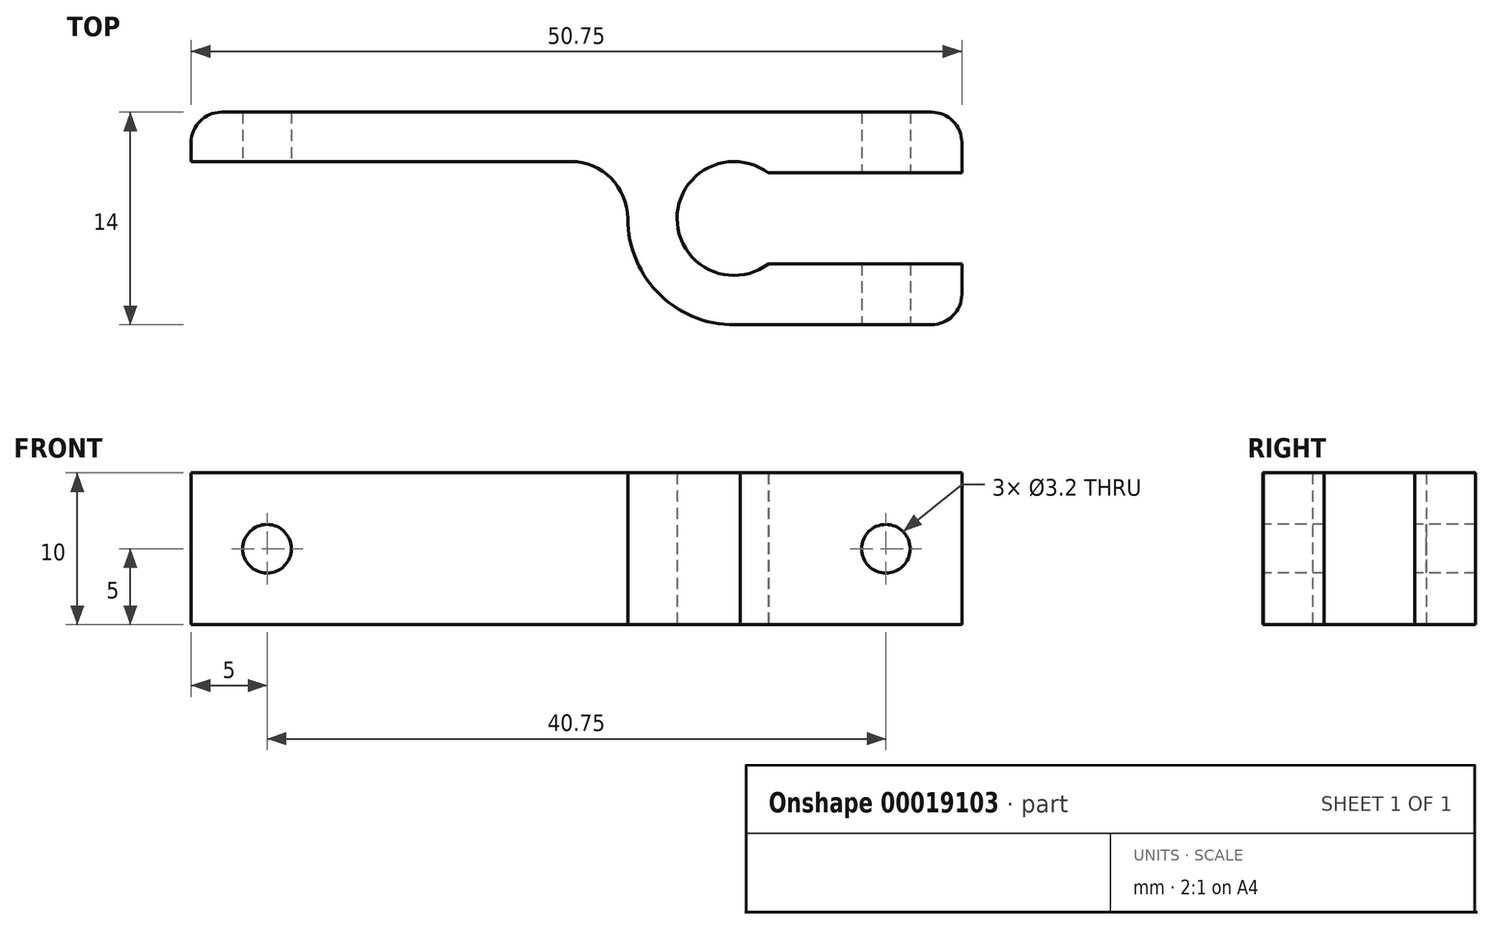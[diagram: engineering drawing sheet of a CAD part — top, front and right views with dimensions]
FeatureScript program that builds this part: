
annotation { "Feature Type Name" : "Feature", "Feature Type Description" : "" }
export const myFeature = defineFeature(function(context is Context, id is Id, definition is map)
    precondition{}
    {
        {
            var Q0;
            Q0=qCreatedBy(makeId("Top.planeOp"),FACE);
            var sketch = newSketch(context, id + "F0", { "sketchPlane" : qUnion([Q0])});
            skArc(sketch, "E0", {"start": v(-12.75, 8.6) * mm, "mid": v(-18.75, 5.59) * mm, "end": v(-12.73, 2.6) * mm});
            skArc(sketch, "E1", {"start": v(-22, 5.6) * mm, "mid": v(-19.8, 0.5) * mm, "end": v(-14.6, -1.4) * mm});
            skLineSegment(sketch, "E2.bottom", {"start": v(-15, 12.6) * mm, "end": v(-50.75, 12.6) * mm});
            skLineSegment(sketch, "E2.top", {"start": v(-25.75, 9.35) * mm, "end": v(-50.75, 9.35) * mm});
            skLineSegment(sketch, "E2.left", {"start": v(-15, 12.6) * mm, "end": v(-15, 9.35) * mm});
            skLineSegment(sketch, "E2.right", {"start": v(-50.75, 12.6) * mm, "end": v(-50.75, 9.35) * mm});
            skArc(sketch, "E3", {"start": v(-22, 5.6) * mm, "mid": v(-23.1, 8.25) * mm, "end": v(-25.75, 9.35) * mm});
            skLineSegment(sketch, "E4.bottom", {"start": v(-15, 12.6) * mm, "end": v(0, 12.6) * mm});
            skLineSegment(sketch, "E4.top", {"start": v(-15, -1.4) * mm, "end": v(0, -1.4) * mm});
            skLineSegment(sketch, "E4.right", {"start": v(0, 12.6) * mm, "end": v(0, 8.6) * mm});
            skLineSegment(sketch, "E5.bottom", {"start": v(-12.73, 2.6) * mm, "end": v(0, 2.6) * mm});
            skLineSegment(sketch, "E5.top", {"start": v(-12.75, 8.6) * mm, "end": v(0, 8.6) * mm});
            skLineSegment(sketch, "E6.trimOffspring", {"start": v(0, 2.6) * mm, "end": v(0, -1.4) * mm});
            skLineSegment(sketch, "E7.trimOffspring", {"start": v(-15, 1.85) * mm, "end": v(-15, -1.4) * mm});
            skSolve(sketch);
        }
        {
            var Q0;
            Q0 = qSketchRegion(id + "F0", true);
            extrude(context, id + "F1", {"entities" : qUnion([Q0]), "depth" : 10 * mm});
        }
        {
            var Q0;
            Q0=makeQuery(id+"F1.opExtrude","SWEPT_FACE",FACE,{"disambiguationData":[OSD([sQuery(id+"F0.wireOp",EDGE,"E4.top")])]});
            var sketch = newSketch(context, id + "F2", { "sketchPlane" : qUnion([Q0])});
            skCircle(sketch, "E8", {"center": v(-5, 5) * mm, "radius": 1.6 * mm});
            skCircle(sketch, "E9", {"center": v(-45.75, 5) * mm, "radius": 1.6 * mm});
            skPoint(sketch, "E10", {"position": v(-50.75, 5) * mm});
            skSolve(sketch);
        }
        {
            var Q0;
            Q0 = qSketchRegion(id + "F2", true);
            extrude(context, id + "F3", {"entities" : qUnion([Q0]), "operationType" : NewBodyOperationType.REMOVE, "endBound" : BoundingType.THROUGH_ALL, "oppositeDirection" : true, "depth" : 25 * mm});
        }
        {
            var Q0;
            Q0=makeQuery(id+"F1.opExtrude","SWEPT_EDGE",EDGE,{"disambiguationData":[OSD([sQuery(id+"F0.wireOp",EDGE,"E2.bottom"),sQuery(id+"F0.wireOp",EDGE,"E2.right")])]});
            var Q1;
            Q1=makeQuery(id+"F1.opExtrude","SWEPT_EDGE",EDGE,{"disambiguationData":[OSD([sQuery(id+"F0.wireOp",EDGE,"E4.bottom"),sQuery(id+"F0.wireOp",EDGE,"E4.right")])]});
            var Q2;
            Q2=makeQuery(id+"F1.opExtrude","SWEPT_EDGE",EDGE,{"disambiguationData":[OSD([sQuery(id+"F0.wireOp",EDGE,"E4.top"),sQuery(id+"F0.wireOp",EDGE,"E6.trimOffspring")])]});
            fillet(context, id + "F4", {"entities" : qUnion([Q0, Q1, Q2]), "radius" : 2 * mm, "tangentPropagation" : true, "allowEdgeOverflow" : false});
        }
    });
